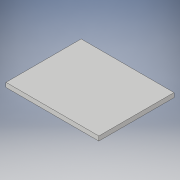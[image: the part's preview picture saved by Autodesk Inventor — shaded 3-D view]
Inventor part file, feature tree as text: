
AUTODESK INVENTOR PART (.ipt)
format: ipt  version: 2019.3 (Build 233278000, 278)  size: 89,600 bytes
history: native  units: mm
features: other x1, extrude x1, sketch x1
ambient origin geometry x8: Origin, YZ Plane, XZ Plane, XY Plane, X Axis, Y Axis, Z Axis, Center Point
bodies: Body1 (feature_tree)
feature tree (3):
  other  "ソリッド1"
  extrude  "押し出し1"  Depth=2100.0mm
  sketch  "スケッチ1"
